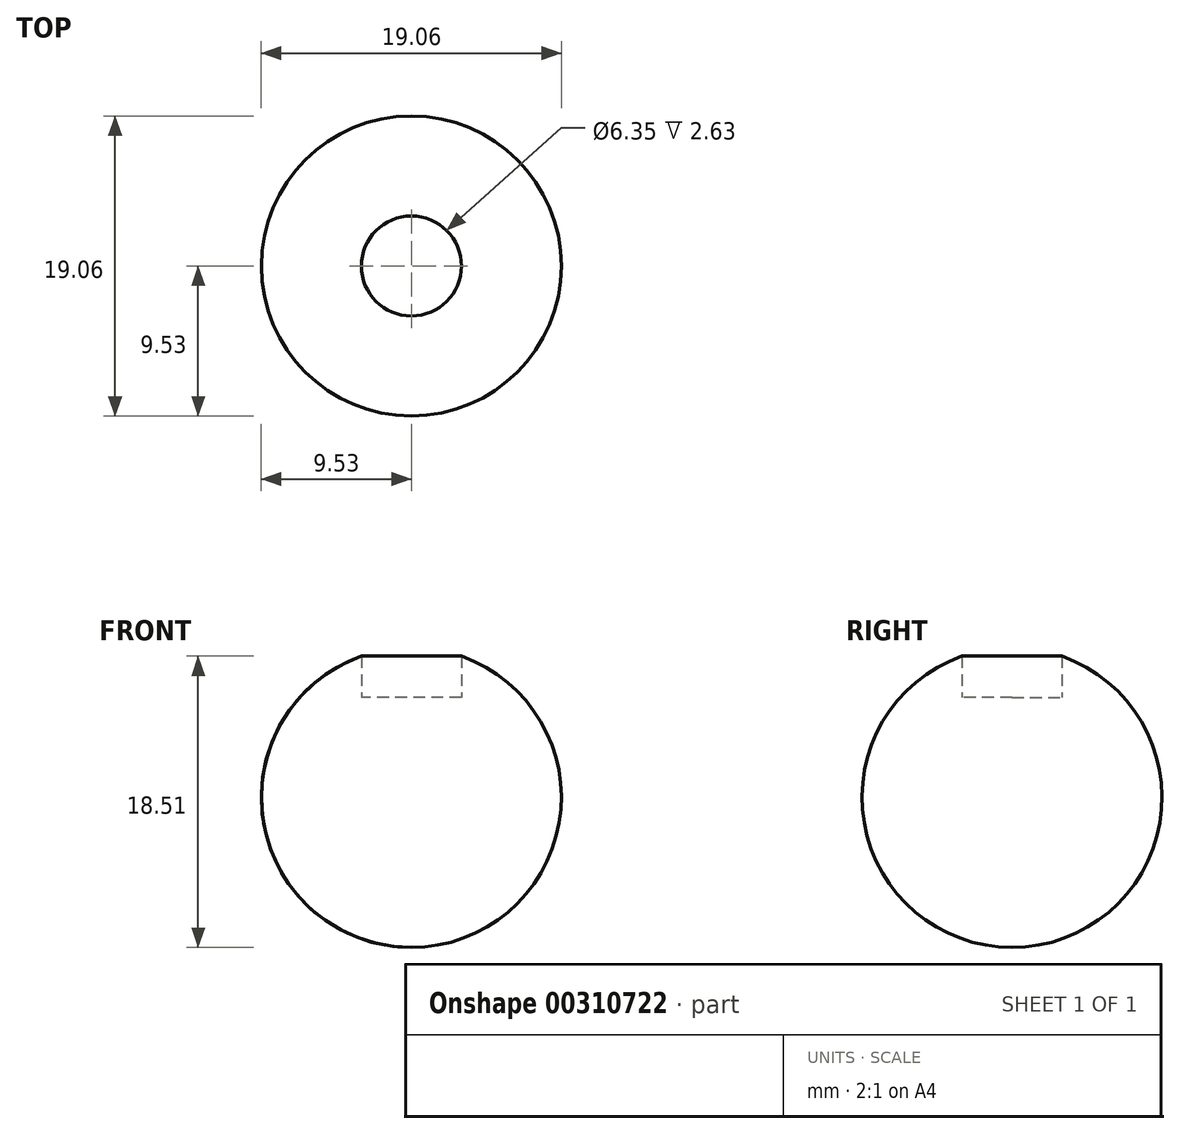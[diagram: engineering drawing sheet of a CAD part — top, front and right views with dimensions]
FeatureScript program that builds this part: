
annotation { "Feature Type Name" : "Feature", "Feature Type Description" : "" }
export const myFeature = defineFeature(function(context is Context, id is Id, definition is map)
    precondition{}
    {
        {
            var Q0;
            Q0=qCreatedBy(makeId("Top.planeOp"),FACE);
            var sketch = newSketch(context, id + "F0", { "sketchPlane" : qUnion([Q0])});
            skCircle(sketch, "E0", {"center": v(0, 0) * mm, "radius": 9.53 * mm});
            skSolve(sketch);
        }
        {
            var Q0;
            Q0=qCreatedBy(makeId("Front.planeOp"),FACE);
            var sketch = newSketch(context, id + "F1", { "sketchPlane" : qUnion([Q0])});
            skArc(sketch, "E1", {"start": v(0, 9.53) * mm, "mid": v(-9.53, 0) * mm, "end": v(0, -9.53) * mm});
            skLineSegment(sketch, "E2", {"start": v(0, -9.53) * mm, "end": v(0, 9.53) * mm});
            skSolve(sketch);
        }
        {
            var Q0;
            Q0=makeQuery(id+"F1.imprint","IMPRINT",FACE,{"disambiguationData":[TD([[makeQuery(id+"F1.imprint","IMPRINT",EDGE,{"derivedFrom":sQuery(id+"F1.wireOp",EDGE,"E1")}),1.0]])]});
            var Q1;
            Q1=sQuery(id+"F0.wireOp",EDGE,"E0");
            revolve(context, id + "F2", {"entities" : qUnion([Q0]), "axis" : qUnion([Q1]), "revolveType" : RevolveType.FULL});
        }
        {
            var Q0;
            Q0=qCreatedBy(makeId("Top.planeOp"),FACE);
            cPlane(context, id + "F3", {"entities" : qUnion([Q0]), "cplaneType" : CPlaneType.OFFSET, "offset" : 6.35 * mm, "width" : 152.4 * mm, "height" : 152.4 * mm});
        }
        {
            var Q0;
            Q0=qCreatedBy(id+"F3.planeOp",FACE);
            var sketch = newSketch(context, id + "F4", { "sketchPlane" : qUnion([Q0])});
            skCircle(sketch, "E3", {"center": v(0, 0) * mm, "radius": 3.18 * mm});
            skSolve(sketch);
        }
        {
            var Q0;
            Q0=makeQuery(id+"F4.imprint","IMPRINT",FACE,{"disambiguationData":[TD([[makeQuery(id+"F4.imprint","IMPRINT",EDGE,{"derivedFrom":sQuery(id+"F4.wireOp",EDGE,"E3")}),1.0]])]});
            extrude(context, id + "F5", {"entities" : qUnion([Q0]), "depth" : 25.4 * mm});
        }
        {
            var Q0;
            Q0=makeQuery(id+"F5.opExtrude","SWEPT_BODY",BODY,{"disambiguationData":[OSD([sQuery(id+"F4.wireOp",EDGE,"E3")])]});
            var Q1;
            Q1=makeQuery(id+"F2.opRevolve","SWEPT_BODY",BODY,{"disambiguationData":[OSD([sQuery(id+"F1.wireOp",EDGE,"E1"),sQuery(id+"F1.wireOp",EDGE,"E2")])]});
            booleanBodies(context, id + "F6", {"operationType" : BooleanOperationType.SUBTRACTION, "tools" : qUnion([Q0]), "targets" : qUnion([Q1])});
        }
    });
